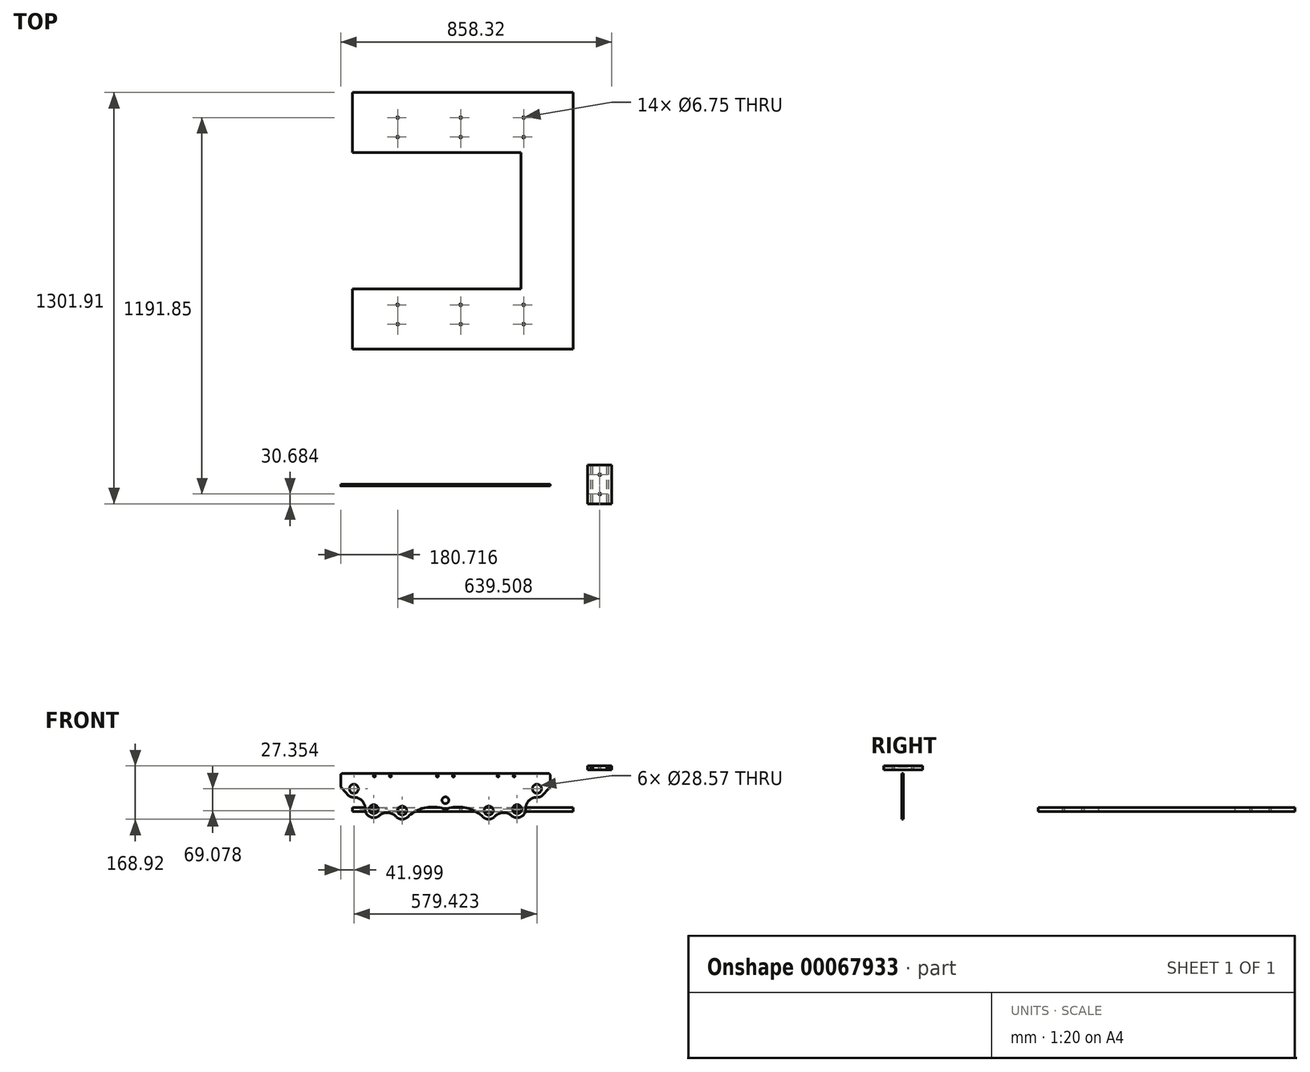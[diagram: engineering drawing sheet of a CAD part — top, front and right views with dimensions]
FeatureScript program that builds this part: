
annotation { "Feature Type Name" : "Feature", "Feature Type Description" : "" }
export const myFeature = defineFeature(function(context is Context, id is Id, definition is map)
    precondition{}
    {
        {
            var Q0;
            Q0=qCreatedBy(makeId("Front.planeOp"),FACE);
            var sketch = newSketch(context, id + "F0", { "sketchPlane" : qUnion([Q0])});
            skLineSegment(sketch, "E0", {"start": v(678.42, -37.96) * mm, "end": v(-454, -37.96) * mm, "construction": true});
            skLineSegment(sketch, "E1", {"start": v(678.42, -33.2) * mm, "end": v(-454, -33.2) * mm, "construction": true});
            skLineSegment(sketch, "E2", {"start": v(678.42, -31.61) * mm, "end": v(-454, -31.61) * mm, "construction": true});
            skCircle(sketch, "E3", {"center": v(289.71, 72.4) * mm, "radius": 41.28 * mm, "construction": true});
            skLineSegment(sketch, "E4", {"start": v(0, -37.96) * mm, "end": v(0, 332.54) * mm, "construction": true});
            skCircle(sketch, "E5", {"center": v(136.96, 3.31) * mm, "radius": 14.29 * mm});
            skCircle(sketch, "E6", {"center": v(226.87, 8.08) * mm, "radius": 14.29 * mm});
            skCircle(sketch, "E7", {"center": v(289.71, 72.4) * mm, "radius": 14.29 * mm});
            skLineSegment(sketch, "E8", {"start": v(289.71, 72.4) * mm, "end": v(0, 72.4) * mm, "construction": true});
            skArc(sketch, "E9.filletArc", {"start": v(327.55, 74.15) * mm, "mid": v(330.62, 78.41) * mm, "end": v(331.7, 83.55) * mm});
            skCircle(sketch, "E10", {"center": v(217.4, 112.75) * mm, "radius": 3.18 * mm});
            skCircle(sketch, "E11", {"center": v(166.6, 112.75) * mm, "radius": 3.18 * mm});
            skCircle(sketch, "E12", {"center": v(25.4, 112.75) * mm, "radius": 3.18 * mm});
            skLineSegment(sketch, "E13.rect.bottom", {"start": v(526.61, 144.88) * mm, "end": v(450.41, 144.88) * mm});
            skLineSegment(sketch, "E13.rect.top", {"start": v(526.61, 132.18) * mm, "end": v(450.41, 132.18) * mm});
            skLineSegment(sketch, "E13.rect.left", {"start": v(526.61, 144.88) * mm, "end": v(526.61, 132.18) * mm});
            skLineSegment(sketch, "E13.rect.right", {"start": v(450.41, 144.88) * mm, "end": v(450.41, 132.18) * mm});
            skPoint(sketch, "E13.rect.middle", {"position": v(488.51, 138.53) * mm});
            skLineSegment(sketch, "E14", {"start": v(435.23, 138.53) * mm, "end": v(583.4, 138.53) * mm, "construction": true});
            skPoint(sketch, "E14.startSnap0", {"position": v(450.41, 138.53) * mm});
            skLineSegment(sketch, "E15", {"start": v(488.51, 159.76) * mm, "end": v(488.51, 110.45) * mm, "construction": true});
            skPoint(sketch, "E15.startSnap0", {"position": v(488.51, 144.88) * mm});
            skCircle(sketch, "E16", {"center": v(513.91, 138.53) * mm, "radius": 3.37 * mm});
            skCircle(sketch, "E17.MirrorC", {"center": v(463.11, 138.53) * mm, "radius": 3.37 * mm});
            skLineSegment(sketch, "E18", {"start": v(331.7, 83.55) * mm, "end": v(331.7, 114.54) * mm});
            skPoint(sketch, "E19.visualSharp", {"position": v(331.7, 119.1) * mm});
            skArc(sketch, "E19.filletArc", {"start": v(331.7, 114.54) * mm, "mid": v(329.85, 119.03) * mm, "end": v(325.36, 120.9) * mm});
            skPoint(sketch, "E20.third.point", {"position": v(216.25, -1.48) * mm});
            skPoint(sketch, "E21.orphan", {"position": v(0, -22.86) * mm});
            skCircle(sketch, "E22", {"center": v(289.71, 72.4) * mm, "radius": 21 * mm, "construction": true});
            skLineSegment(sketch, "E23", {"start": v(138.63, -17.62) * mm, "end": v(228.14, -14.1) * mm, "construction": true});
            skLineSegment(sketch, "E24", {"start": v(307.87, 61.84) * mm, "end": v(242, -6.5) * mm, "construction": true});
            skCircle(sketch, "E25", {"center": v(0, 35.95) * mm, "radius": 41.28 * mm, "construction": true});
            skCircle(sketch, "E26.MirrorC", {"center": v(0, 35.95) * mm, "radius": 10.7 * mm});
            skCircle(sketch, "E27", {"center": v(226.87, 8.08) * mm, "radius": 21 * mm, "construction": true});
            skCircle(sketch, "E28", {"center": v(136.96, 3.31) * mm, "radius": 21 * mm, "construction": true});
            skCircle(sketch, "E29", {"center": v(0, 35.95) * mm, "radius": 21 * mm, "construction": true});
            skCircle(sketch, "E30", {"center": v(136.96, 3.31) * mm, "radius": 41.28 * mm, "construction": true});
            skCircle(sketch, "E31", {"center": v(226.87, 8.08) * mm, "radius": 41.28 * mm, "construction": true});
            skLineSegment(sketch, "E32", {"start": v(136.96, 3.31) * mm, "end": v(226.87, 8.08) * mm, "construction": true});
            skLineSegment(sketch, "E33", {"start": v(226.87, 8.08) * mm, "end": v(289.71, 72.4) * mm, "construction": true});
            skLineSegment(sketch, "E34", {"start": v(325.36, 120.9) * mm, "end": v(0, 120.9) * mm});
            skLineSegment(sketch, "E35.MirrorCS", {"start": v(-325.36, 120.9) * mm, "end": v(0, 120.9) * mm});
            skArc(sketch, "E36.MirrorCS", {"start": v(-331.7, 114.54) * mm, "mid": v(-329.85, 119.03) * mm, "end": v(-325.36, 120.9) * mm});
            skLineSegment(sketch, "E37.MirrorCS", {"start": v(-331.7, 83.55) * mm, "end": v(-331.7, 114.54) * mm});
            skCircle(sketch, "E38.MirrorC", {"center": v(-226.87, 8.08) * mm, "radius": 14.29 * mm});
            skCircle(sketch, "E39.MirrorC", {"center": v(-136.96, 3.31) * mm, "radius": 14.29 * mm});
            skCircle(sketch, "E40.MirrorC", {"center": v(-25.4, 112.75) * mm, "radius": 3.18 * mm});
            skCircle(sketch, "E41.MirrorC", {"center": v(-173.98, 112.75) * mm, "radius": 3.18 * mm});
            skCircle(sketch, "E42.MirrorC", {"center": v(-224.78, 112.75) * mm, "radius": 3.18 * mm});
            skCircle(sketch, "E43.MirrorC", {"center": v(-289.71, 72.4) * mm, "radius": 14.29 * mm});
            skLineSegment(sketch, "E44", {"start": v(-5.23, 15.6) * mm, "end": v(132.1, -17.11) * mm, "construction": true});
            skArc(sketch, "E45.0", {"start": v(211.8, -14.74) * mm, "mid": v(238.96, -16.46) * mm, "end": v(254.15, 6.12) * mm});
            skArc(sketch, "E46.0", {"start": v(115.05, -13.05) * mm, "mid": v(134.31, -23.9) * mm, "end": v(155.31, -16.96) * mm});
            skArc(sketch, "E47", {"start": v(211.8, -14.74) * mm, "mid": v(183.05, -3.16) * mm, "end": v(155.31, -16.96) * mm});
            skArc(sketch, "E48.0", {"start": v(291.75, 45.12) * mm, "mid": v(299.56, 46.88) * mm, "end": v(306.53, 50.83) * mm});
            skLineSegment(sketch, "E49", {"start": v(327.55, 74.15) * mm, "end": v(306.53, 50.83) * mm});
            skArc(sketch, "E50", {"start": v(291.75, 45.12) * mm, "mid": v(263.8, 34.43) * mm, "end": v(254.15, 6.12) * mm});
            skArc(sketch, "E51.0", {"start": v(-12.18, 11.46) * mm, "mid": v(0, 8.6) * mm, "end": v(12.18, 11.46) * mm});
            skArc(sketch, "E52", {"start": v(115.05, -13.05) * mm, "mid": v(66.56, 11.56) * mm, "end": v(12.18, 11.46) * mm});
            skLineSegment(sketch, "E53", {"start": v(136.96, 3.31) * mm, "end": v(0, 35.95) * mm, "construction": true});
            skArc(sketch, "E54.MirrorCS", {"start": v(-115.05, -13.05) * mm, "mid": v(-66.56, 11.56) * mm, "end": v(-12.18, 11.46) * mm});
            skArc(sketch, "E55.MirrorCS", {"start": v(-115.05, -13.05) * mm, "mid": v(-134.31, -23.9) * mm, "end": v(-155.31, -16.96) * mm});
            skArc(sketch, "E56.MirrorCS", {"start": v(-211.8, -14.74) * mm, "mid": v(-183.05, -3.16) * mm, "end": v(-155.31, -16.96) * mm});
            skArc(sketch, "E57.MirrorCS", {"start": v(-211.8, -14.74) * mm, "mid": v(-238.96, -16.46) * mm, "end": v(-254.15, 6.12) * mm});
            skArc(sketch, "E58.MirrorCS", {"start": v(-291.75, 45.12) * mm, "mid": v(-263.8, 34.43) * mm, "end": v(-254.15, 6.12) * mm});
            skArc(sketch, "E59.MirrorCS", {"start": v(-291.75, 45.12) * mm, "mid": v(-299.56, 46.88) * mm, "end": v(-306.53, 50.83) * mm});
            skLineSegment(sketch, "E60.MirrorCS", {"start": v(-327.55, 74.15) * mm, "end": v(-306.53, 50.83) * mm});
            skArc(sketch, "E61.MirrorCS", {"start": v(-327.55, 74.15) * mm, "mid": v(-330.62, 78.41) * mm, "end": v(-331.7, 83.55) * mm});
            skCircle(sketch, "E62.0", {"center": v(289.71, 72.4) * mm, "radius": 20.64 * mm, "construction": true});
            skSolve(sketch);
        }
        {
            var Q0;
            Q0=makeQuery(id+"F0.imprint","IMPRINT",FACE,{"disambiguationData":[TD([[makeQuery(id+"F0.imprint","IMPRINT",EDGE,{"derivedFrom":sQuery(id+"F0.wireOp",EDGE,"E6")}),-1.0]])]});
            extrude(context, id + "F1", {"entities" : qUnion([Q0]), "depth" : 4.76 * mm});
        }
        {
            var Q0;
            Q0=makeQuery(id+"F0.imprint","IMPRINT",FACE,{"disambiguationData":[TD([[makeQuery(id+"F0.imprint","IMPRINT",EDGE,{"derivedFrom":sQuery(id+"F0.wireOp",EDGE,"E13.rect.bottom")}),1.0]])]});
            extrude(context, id + "F2", {"entities" : qUnion([Q0]), "endBound" : BoundingType.SYMMETRIC, "depth" : 122.75 * mm});
        }
        {
            var Q0;
            Q0=makeQuery(id+"F2.opExtrude","SWEPT_FACE",FACE,{"disambiguationData":[OSD([sQuery(id+"F0.wireOp",EDGE,"E13.rect.bottom")])]});
            var sketch = newSketch(context, id + "F3", { "sketchPlane" : qUnion([Q0])});
            skCircle(sketch, "E63", {"center": v(488.51, -30.69) * mm, "radius": 3.37 * mm});
            skLineSegment(sketch, "E64", {"start": v(488.51, 61.37) * mm, "end": v(488.51, -61.37) * mm, "construction": true});
            skLineSegment(sketch, "E65", {"start": v(450.41, 0) * mm, "end": v(526.61, 0) * mm, "construction": true});
            skLineSegment(sketch, "E66", {"start": v(526.61, 0) * mm, "end": v(526.61, -61.37) * mm, "construction": true});
            skLineSegment(sketch, "E67", {"start": v(526.61, -30.69) * mm, "end": v(450.41, -30.69) * mm, "construction": true});
            skCircle(sketch, "E68.MirrorC", {"center": v(488.51, 30.69) * mm, "radius": 3.37 * mm});
            skSolve(sketch);
        }
        {
            var Q0;
            Q0 = qSketchRegion(id + "F3", true);
            extrude(context, id + "F4", {"entities" : qUnion([Q0]), "operationType" : NewBodyOperationType.REMOVE, "endBound" : BoundingType.THROUGH_ALL, "oppositeDirection" : true, "depth" : 25.4 * mm});
        }
        {
            var Q0;
            Q0=qCreatedBy(makeId("Top.planeOp"),FACE);
            var sketch = newSketch(context, id + "F5", { "sketchPlane" : qUnion([Q0])});
            skLineSegment(sketch, "E69.bottom", {"start": v(-294.53, 1240.54) * mm, "end": v(403.97, 1240.54) * mm});
            skLineSegment(sketch, "E69.left", {"start": v(-294.53, 1240.54) * mm, "end": v(-294.53, 1050.04) * mm});
            skLineSegment(sketch, "E69.right", {"start": v(403.97, 1240.54) * mm, "end": v(403.97, 427.74) * mm});
            skLineSegment(sketch, "E70", {"start": v(-294.53, 1050.04) * mm, "end": v(238.87, 1050.04) * mm});
            skLineSegment(sketch, "E71", {"start": v(238.87, 1050.04) * mm, "end": v(238.87, 618.24) * mm});
            skLineSegment(sketch, "E72", {"start": v(238.87, 618.24) * mm, "end": v(-294.53, 618.24) * mm});
            skLineSegment(sketch, "E73", {"start": v(-294.53, 618.24) * mm, "end": v(-294.53, 427.74) * mm});
            skCircle(sketch, "E74", {"center": v(247.74, 507.12) * mm, "radius": 3.37 * mm});
            skCircle(sketch, "E75.MirrorC", {"center": v(247.74, 568.48) * mm, "radius": 3.37 * mm});
            skCircle(sketch, "E76", {"center": v(48.37, 507.12) * mm, "radius": 3.37 * mm});
            skCircle(sketch, "E77.MirrorC", {"center": v(48.37, 568.48) * mm, "radius": 3.37 * mm});
            skCircle(sketch, "E78", {"center": v(-151, 507.12) * mm, "radius": 3.37 * mm});
            skCircle(sketch, "E79.MirrorC", {"center": v(-151, 568.48) * mm, "radius": 3.37 * mm});
            skLineSegment(sketch, "E80.bottom", {"start": v(-283.34, 605.54) * mm, "end": v(380.08, 605.54) * mm, "construction": true});
            skLineSegment(sketch, "E80.left", {"start": v(-283.34, 605.54) * mm, "end": v(-283.34, 599.2) * mm, "construction": true});
            skLineSegment(sketch, "E80.right", {"start": v(380.08, 605.54) * mm, "end": v(380.08, 599.2) * mm, "construction": true});
            skLineSegment(sketch, "E81.bottom", {"start": v(-283.33, 476.43) * mm, "end": v(380.1, 476.43) * mm, "construction": true});
            skLineSegment(sketch, "E81.top", {"start": v(-283.33, 470.08) * mm, "end": v(380.1, 470.08) * mm, "construction": true});
            skLineSegment(sketch, "E82", {"start": v(-283.33, 476.43) * mm, "end": v(-283.33, 470.08) * mm});
            skLineSegment(sketch, "E83", {"start": v(380.1, 476.43) * mm, "end": v(380.1, 470.08) * mm});
            skLineSegment(sketch, "E84.top", {"start": v(404.77, 440.42) * mm, "end": v(-294.53, 440.42) * mm, "construction": true});
            skLineSegment(sketch, "E84.left", {"start": v(403.97, 427.74) * mm, "end": v(404.77, 440.42) * mm});
            skLineSegment(sketch, "E85", {"start": v(-294.53, 523) * mm, "end": v(663.27, 523) * mm, "construction": true});
            skLineSegment(sketch, "E86", {"start": v(-283.34, 523) * mm, "end": v(-346.9, 523) * mm, "construction": true});
            skLineSegment(sketch, "E87", {"start": v(391.27, 1240.54) * mm, "end": v(391.27, 427.74) * mm, "construction": true});
            skLineSegment(sketch, "E88", {"start": v(238.87, 834.14) * mm, "end": v(403.97, 834.14) * mm, "construction": true});
            skCircle(sketch, "E89.MirrorC", {"center": v(-151, 1099.8) * mm, "radius": 3.37 * mm});
            skCircle(sketch, "E90.MirrorC", {"center": v(-151, 1161.17) * mm, "radius": 3.37 * mm});
            skCircle(sketch, "E91.MirrorC", {"center": v(48.37, 1099.8) * mm, "radius": 3.37 * mm});
            skCircle(sketch, "E92.MirrorC", {"center": v(48.37, 1161.17) * mm, "radius": 3.37 * mm});
            skCircle(sketch, "E93.MirrorC", {"center": v(247.74, 1161.17) * mm, "radius": 3.37 * mm});
            skCircle(sketch, "E94.MirrorC", {"center": v(247.74, 1099.8) * mm, "radius": 3.37 * mm});
            skLineSegment(sketch, "E95", {"start": v(-283.34, 599.2) * mm, "end": v(380.08, 599.2) * mm, "construction": true});
            skLineSegment(sketch, "E96", {"start": v(-294.53, 427.74) * mm, "end": v(403.97, 427.74) * mm});
            skSolve(sketch);
        }
        {
            var Q0;
            Q0 = qSketchRegion(id + "F5", true);
            extrude(context, id + "F6", {"entities" : qUnion([Q0]), "depth" : 12.7 * mm});
        }
    });
